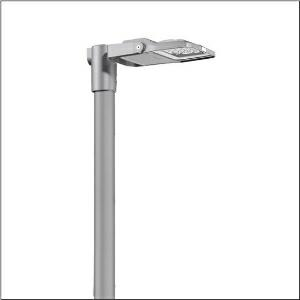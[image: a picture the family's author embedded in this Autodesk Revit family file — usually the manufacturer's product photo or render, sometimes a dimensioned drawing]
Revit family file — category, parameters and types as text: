
# Revit family: floodlight_fl_21_iq_micro___pl43_5xa7762a2a3a_62d6
name_source: partatom
category: Lighting Fixtures
units: mm (PartAtom-declared; Revit-internal decimal feet)

## family parameters
Cut with Voids When Loaded = No
Host = Face
Light Source = No
Part Type = Normal
Room Calculation Point = No
Round Connector Dimension = Use Diameter
Shared = No

## types (1)
- --- (1 x LED, 3040 lm, 23.1 W, 3000K)
    Apparent Load = 23 VA
    CIE Flux Codes = 29 80 99 100 100
    Color Rendering = 70
    Color Temperature = 3000K
    Default Elevation = 1800 mm
    Description = Floodlight FL 21 iQ micro, floodlight, primary light control with lens, of PMMA, primary optical cover: protective disc, of toughened safety glass, transparent, light distribution: PL43, light emission: direct distribution, installation type: surface-mounted, LED, High Power LED, rated luminous flux: 3.040lm, luminous efficacy: 132lm/W, light colour: 730, colour temperature: 3000K, control gear: iQ Street-Remote/DALI, control: Auto-Match, Temp-Guard, Night-Set, Smart-Wire, Desk-Remote (wireless, voltage-free reading and setting of iQ features in the workshop via application-optimized NFC function/RFID function), optimised constant luminous flux control (CLO 2.0), Street-Remote, with terminal, 6-pole, mains connection: 220..240V, AC, 50/60Hz, start of lifetime: 23W, end of service life: 24W, reduction: 11W, luminaire housing, of diecast aluminium, powder-coated, Siteco® metallic grey (DB 702S), corrosivity category C5 mid according to DIN EN ISO 12944, suitable for swimming pools, chlorine-resistant, sealing non-destructively replaceable, please order mast flange separately, mast bracket, of steel, galvanised, powder-coated, Siteco® metallic grey (DB 702S), protection rating (complete): IP66, insulation class (complete): insulation class II (safety insulation), certification: CE, ENEC, VDE, protection symbol: D, impact resistance: IK07, permissible operating ambient temperature: -40..+40°C, permissible operating ambient temperature for outdoor applications: -40..+50°C, standard: DIN EN 12944, LABS conformity tested according to VDMA 24364:2018-05, packaging unit: 1 piece

Light Distribution: PL43
    Height = 65 mm
    Lamp = 1 x LED
    Lamp Light Flux = 3040 lm
    Lamp Power = 23.1 W
    Lamp count = 1
    Length = 312 mm
    Luminous efficacy = 132 lm/W
    Manufacturer = Siteco
    ModVariant = No
    Model = 5XA7762A2A3A
    Number of Poles = 1
    OnlyDefault = Yes
    Power Factor = 1
    Product Name = Floodlight FL 21 iQ micro | PL43
    Product group = floodlight | pylon annexe
    ProductGroupID = 6200
    Protection Class = Protection class II
    Protection Degree = IP 66
    RLX_Detail_Level = 1
    RLX_Emergency_Light_Flux = 0 lm
    RLX_Emergency_Type = 0
    RLX_Emergency_Type_DB = No
    RlxData = <blob elided: 101925 chars, md5=e5610dd4>
    Socket = socket
    Standby Power = 0 W
    System Light Flux = 3040 lm
    System Power = 23 W
    Type Comments = factory setting: luminous flux: 100 % | dim-lin: 254 | 455 mA
    Type Image = l_1007121.jpg
    URL = http://relux.com
    VarID = @adj_176576
    Voltage = 0 V
    Weight = 0.00 kg
    Width = 230 mm

## geometry (parser evidence)
native form markers: Blend x4, Sweep x12
no freeform markers — native parametric forms only
